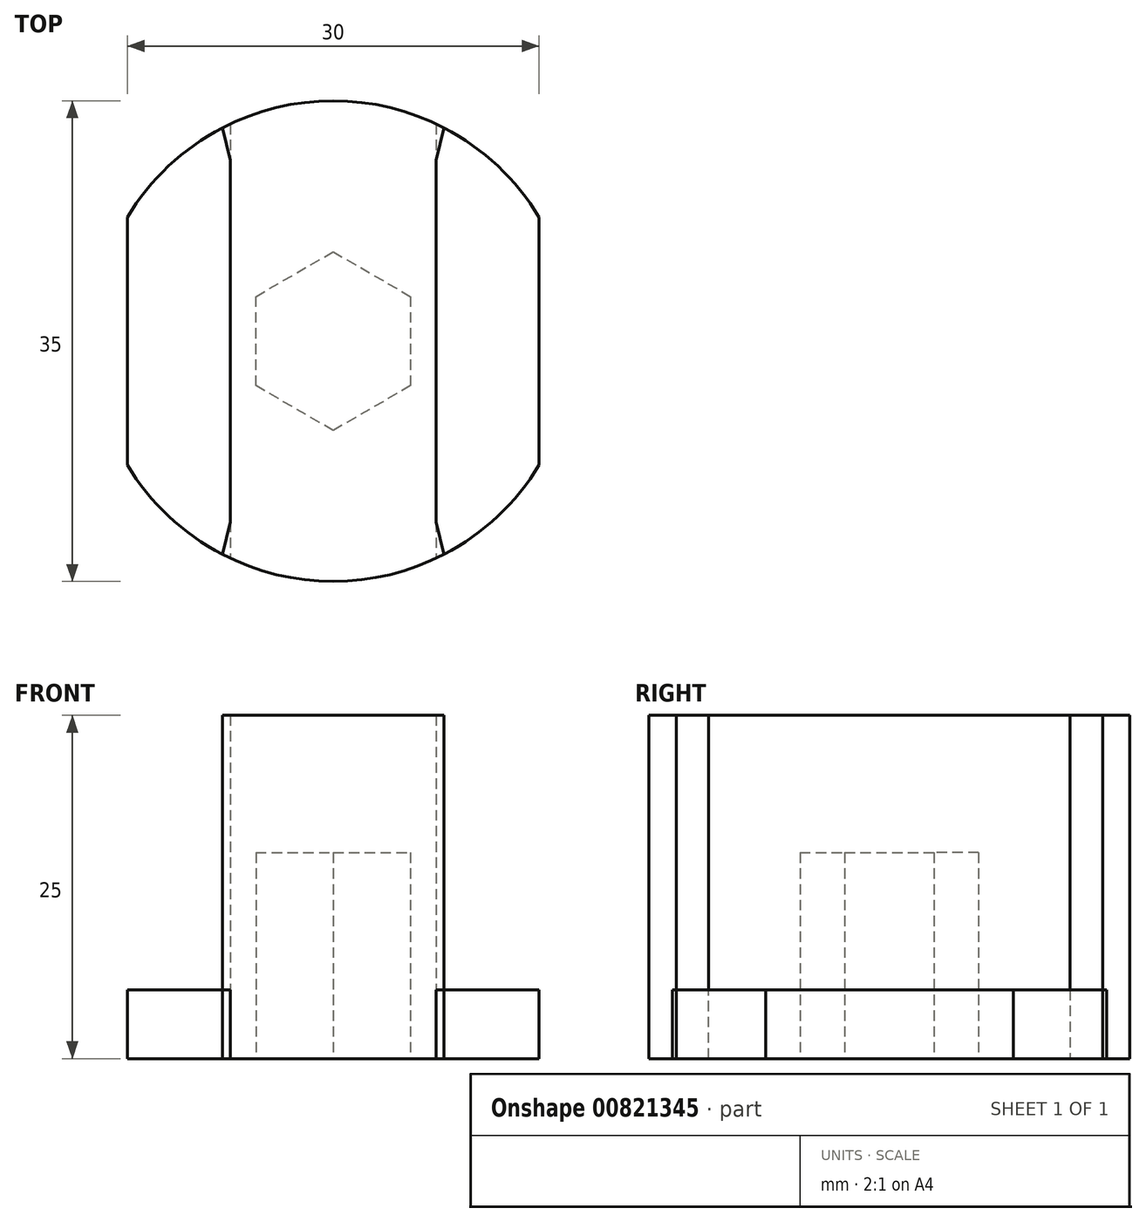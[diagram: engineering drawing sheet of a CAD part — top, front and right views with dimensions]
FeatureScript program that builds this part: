
annotation { "Feature Type Name" : "Feature", "Feature Type Description" : "" }
export const myFeature = defineFeature(function(context is Context, id is Id, definition is map)
    precondition{}
    {
        {
            var Q0;
            Q0=qCreatedBy(makeId("Top.planeOp"),FACE);
            var sketch = newSketch(context, id + "F0", { "sketchPlane" : qUnion([Q0])});
            skCircle(sketch, "E0", {"center": v(0, 0) * mm, "radius": 17.5 * mm});
            skLineSegment(sketch, "E1.bottom", {"start": v(7.5, 20) * mm, "end": v(-7.5, 20) * mm});
            skLineSegment(sketch, "E1.top", {"start": v(7.5, -20) * mm, "end": v(-7.5, -20) * mm});
            skLineSegment(sketch, "E1.left", {"start": v(7.5, 20) * mm, "end": v(7.5, -20) * mm});
            skLineSegment(sketch, "E1.right", {"start": v(-7.5, 20) * mm, "end": v(-7.5, -20) * mm});
            skLineSegment(sketch, "E2.bottom", {"start": v(15, 20) * mm, "end": v(-15, 20) * mm});
            skLineSegment(sketch, "E2.top", {"start": v(15, -20) * mm, "end": v(-15, -20) * mm});
            skLineSegment(sketch, "E2.left", {"start": v(15, 20) * mm, "end": v(15, -20) * mm});
            skLineSegment(sketch, "E2.right", {"start": v(-15, 20) * mm, "end": v(-15, -20) * mm});
            skLineSegment(sketch, "E3.bottom", {"start": v(23.86, 11.75) * mm, "end": v(-23.86, 11.75) * mm});
            skLineSegment(sketch, "E3.top", {"start": v(23.86, -11.75) * mm, "end": v(-23.86, -11.75) * mm});
            skLineSegment(sketch, "E3.left", {"start": v(23.86, 11.75) * mm, "end": v(23.86, -11.75) * mm});
            skLineSegment(sketch, "E3.right", {"start": v(-23.86, 11.75) * mm, "end": v(-23.86, -11.75) * mm});
            skLineSegment(sketch, "E4", {"start": v(0, 0) * mm, "end": v(0, 6.5) * mm});
            skCircle(sketch, "E5.cCircle", {"center": v(0, 0) * mm, "radius": 6.5 * mm, "construction": true});
            skLineSegment(sketch, "E5.0", {"start": v(0, 6.5) * mm, "end": v(5.63, 3.25) * mm});
            skLineSegment(sketch, "E5.1", {"start": v(5.63, 3.25) * mm, "end": v(5.63, -3.25) * mm});
            skLineSegment(sketch, "E5.2", {"start": v(5.63, -3.25) * mm, "end": v(0, -6.5) * mm});
            skLineSegment(sketch, "E5.3", {"start": v(0, -6.5) * mm, "end": v(-5.63, -3.25) * mm});
            skLineSegment(sketch, "E5.4", {"start": v(-5.63, -3.25) * mm, "end": v(-5.63, 3.25) * mm});
            skLineSegment(sketch, "E5.5", {"start": v(-5.63, 3.25) * mm, "end": v(0, 6.5) * mm});
            skSolve(sketch);
        }
        {
            var Q0;
            {var subQ0=sQuery(id+"F0.wireOp",EDGE,"E2.left");var subQ1=sQuery(id+"F0.wireOp",EDGE,"E0");var subQ2=makeQuery(id+"F0.imprint","INTERSECT",VERTEX,{"disambiguationData":[OD(0.0)],"derivedFrom":[subQ1,subQ0]});Q0=makeQuery(id+"F0.imprint","IMPRINT",FACE,{"disambiguationData":[TD([[makeQuery(id+"F0.imprint","IMPRINT",EDGE,{"disambiguationData":[TD([[subQ2,-1.0]])],"derivedFrom":subQ1}),1.0]])]});}
            var Q1;
            {var subQ0=sQuery(id+"F0.wireOp",EDGE,"E2.right");var subQ1=sQuery(id+"F0.wireOp",EDGE,"E0");var subQ2=makeQuery(id+"F0.imprint","INTERSECT",VERTEX,{"disambiguationData":[OD(0.0)],"derivedFrom":[subQ1,subQ0]});Q1=makeQuery(id+"F0.imprint","IMPRINT",FACE,{"disambiguationData":[TD([[makeQuery(id+"F0.imprint","IMPRINT",EDGE,{"disambiguationData":[TD([[subQ2,1.0]])],"derivedFrom":subQ1}),1.0]])]});}
            var Q2;
            {var subQ0=sQuery(id+"F0.wireOp",EDGE,"E1.right");var subQ1=sQuery(id+"F0.wireOp",EDGE,"E0");var subQ2=makeQuery(id+"F0.imprint","INTERSECT",VERTEX,{"disambiguationData":[OD(0.0)],"derivedFrom":[subQ1,subQ0]});Q2=makeQuery(id+"F0.imprint","IMPRINT",FACE,{"disambiguationData":[TD([[makeQuery(id+"F0.imprint","IMPRINT",EDGE,{"disambiguationData":[TD([[subQ2,-1.0]])],"derivedFrom":subQ1}),1.0]])]});}
            var Q3;
            {var subQ0=sQuery(id+"F0.wireOp",EDGE,"E1.left");var subQ1=sQuery(id+"F0.wireOp",EDGE,"E0");var subQ2=makeQuery(id+"F0.imprint","INTERSECT",VERTEX,{"disambiguationData":[OD(1.0)],"derivedFrom":[subQ1,subQ0]});Q3=makeQuery(id+"F0.imprint","IMPRINT",FACE,{"disambiguationData":[TD([[makeQuery(id+"F0.imprint","IMPRINT",EDGE,{"disambiguationData":[TD([[subQ2,-1.0]])],"derivedFrom":subQ1}),1.0]])]});}
            var Q4;
            {var subQ0=sQuery(id+"F0.wireOp",EDGE,"E3.top");var subQ1=sQuery(id+"F0.wireOp",EDGE,"E0");var subQ2=makeQuery(id+"F0.imprint","INTERSECT",VERTEX,{"disambiguationData":[OD(0.0)],"derivedFrom":[subQ1,subQ0]});Q4=makeQuery(id+"F0.imprint","IMPRINT",FACE,{"disambiguationData":[TD([[makeQuery(id+"F0.imprint","IMPRINT",EDGE,{"disambiguationData":[TD([[subQ2,-1.0]])],"derivedFrom":subQ1}),1.0]])]});}
            var Q5;
            {var subQ0=sQuery(id+"F0.wireOp",EDGE,"E3.bottom");var subQ1=sQuery(id+"F0.wireOp",EDGE,"E0");var subQ2=makeQuery(id+"F0.imprint","INTERSECT",VERTEX,{"disambiguationData":[OD(0.0)],"derivedFrom":[subQ1,subQ0]});Q5=makeQuery(id+"F0.imprint","IMPRINT",FACE,{"disambiguationData":[TD([[makeQuery(id+"F0.imprint","IMPRINT",EDGE,{"disambiguationData":[TD([[subQ2,-1.0]])],"derivedFrom":subQ1}),1.0]])]});}
            extrude(context, id + "F1", {"entities" : qUnion([Q0, Q1, Q2, Q3, Q4, Q5]), "depth" : 5 * mm, "offsetDistance" : 25 * mm});
        }
        {
            var Q0;
            Q0=makeQuery(id+"F0.imprint","IMPRINT",FACE,{"disambiguationData":[TD([[makeQuery(id+"F0.imprint","IMPRINT",EDGE,{"derivedFrom":sQuery(id+"F0.wireOp",EDGE,"VkzLpiYD-BapX-SKoB-1HIT-Cqfo4kMJtnIh.bottom")}),1.0]])]});
            var Q1;
            Q1=makeQuery(id+"F0.imprint","IMPRINT",FACE,{"disambiguationData":[TD([[makeQuery(id+"F0.imprint","IMPRINT",EDGE,{"derivedFrom":sQuery(id+"F0.wireOp",EDGE,"VkzLpiYD-BapX-SKoB-1HIT-Cqfo4kMJtnIh.bottom")}),-1.0]])]});
            var Q2;
            {var subQ0=sQuery(id+"F0.wireOp",EDGE,"E3.bottom");var subQ1=sQuery(id+"F0.wireOp",EDGE,"E1.right");var subQ2=makeQuery(id+"F0.imprint","INTERSECT",VERTEX,{"derivedFrom":[subQ1,subQ0]});Q2=makeQuery(id+"F0.imprint","IMPRINT",FACE,{"disambiguationData":[TD([[makeQuery(id+"F0.imprint","IMPRINT",EDGE,{"disambiguationData":[TD([[subQ2,-1.0]])],"derivedFrom":subQ1}),1.0]])]});}
            var Q3;
            {var subQ9=sQuery(id+"F0.wireOp",EDGE,"VkzLpiYD-BapX-SKoB-1HIT-Cqfo4kMJtnIh.top");Q3=makeQuery(id+"F0.imprint","IMPRINT",FACE,{"disambiguationData":[TD([[makeQuery(id+"F0.imprint","IMPRINT",EDGE,{"derivedFrom":subQ9}),1.0]])]});}
            var Q4;
            {var subQ0=sQuery(id+"F0.wireOp",EDGE,"E3.bottom");var subQ1=sQuery(id+"F0.wireOp",EDGE,"E1.left");var subQ2=makeQuery(id+"F0.imprint","INTERSECT",VERTEX,{"derivedFrom":[subQ1,subQ0]});Q4=makeQuery(id+"F0.imprint","IMPRINT",FACE,{"disambiguationData":[TD([[makeQuery(id+"F0.imprint","IMPRINT",EDGE,{"disambiguationData":[TD([[subQ2,-1.0]])],"derivedFrom":subQ1}),-1.0]])]});}
            var Q5;
            {var subQ0=sQuery(id+"F0.wireOp",EDGE,"E3.bottom");var subQ1=sQuery(id+"F0.wireOp",EDGE,"VkzLpiYD-BapX-SKoB-1HIT-Cqfo4kMJtnIh.left");var subQ2=makeQuery(id+"F0.imprint","INTERSECT",VERTEX,{"derivedFrom":[subQ1,subQ0]});Q5=makeQuery(id+"F0.imprint","IMPRINT",FACE,{"disambiguationData":[TD([[makeQuery(id+"F0.imprint","IMPRINT",EDGE,{"disambiguationData":[TD([[subQ2,-1.0]])],"derivedFrom":subQ1}),-1.0]])]});}
            var Q6;
            {var subQ0=sQuery(id+"F0.wireOp",EDGE,"VkzLpiYD-BapX-SKoB-1HIT-Cqfo4kMJtnIh.top");Q6=makeQuery(id+"F0.imprint","IMPRINT",FACE,{"disambiguationData":[TD([[makeQuery(id+"F0.imprint","IMPRINT",EDGE,{"derivedFrom":subQ0}),-1.0]])]});}
            var Q7;
            {var subQ0=sQuery(id+"F0.wireOp",EDGE,"E3.top");var subQ1=sQuery(id+"F0.wireOp",EDGE,"E0");var subQ2=makeQuery(id+"F0.imprint","INTERSECT",VERTEX,{"disambiguationData":[OD(0.0)],"derivedFrom":[subQ1,subQ0]});Q7=makeQuery(id+"F0.imprint","IMPRINT",FACE,{"disambiguationData":[TD([[makeQuery(id+"F0.imprint","IMPRINT",EDGE,{"disambiguationData":[TD([[subQ2,-1.0]])],"derivedFrom":subQ1}),1.0]])]});}
            var Q8;
            {var subQ0=sQuery(id+"F0.wireOp",EDGE,"E1.right");var subQ1=sQuery(id+"F0.wireOp",EDGE,"E0");var subQ2=makeQuery(id+"F0.imprint","INTERSECT",VERTEX,{"disambiguationData":[OD(0.0)],"derivedFrom":[subQ1,subQ0]});Q8=makeQuery(id+"F0.imprint","IMPRINT",FACE,{"disambiguationData":[TD([[makeQuery(id+"F0.imprint","IMPRINT",EDGE,{"disambiguationData":[TD([[subQ2,-1.0]])],"derivedFrom":subQ1}),1.0]])]});}
            var Q9;
            {var subQ0=sQuery(id+"F0.wireOp",EDGE,"E3.bottom");var subQ1=sQuery(id+"F0.wireOp",EDGE,"E0");var subQ2=makeQuery(id+"F0.imprint","INTERSECT",VERTEX,{"disambiguationData":[OD(0.0)],"derivedFrom":[subQ1,subQ0]});Q9=makeQuery(id+"F0.imprint","IMPRINT",FACE,{"disambiguationData":[TD([[makeQuery(id+"F0.imprint","IMPRINT",EDGE,{"disambiguationData":[TD([[subQ2,-1.0]])],"derivedFrom":subQ1}),1.0]])]});}
            var Q10;
            {var subQ0=sQuery(id+"F0.wireOp",EDGE,"E1.left");var subQ1=sQuery(id+"F0.wireOp",EDGE,"E0");var subQ2=makeQuery(id+"F0.imprint","INTERSECT",VERTEX,{"disambiguationData":[OD(1.0)],"derivedFrom":[subQ1,subQ0]});Q10=makeQuery(id+"F0.imprint","IMPRINT",FACE,{"disambiguationData":[TD([[makeQuery(id+"F0.imprint","IMPRINT",EDGE,{"disambiguationData":[TD([[subQ2,-1.0]])],"derivedFrom":subQ1}),1.0]])]});}
            var Q11;
            {var subQ0=sQuery(id+"F0.wireOp",EDGE,"E1.left");var subQ1=sQuery(id+"F0.wireOp",EDGE,"E0");var subQ2=makeQuery(id+"F0.imprint","INTERSECT",VERTEX,{"disambiguationData":[OD(0.0)],"derivedFrom":[subQ1,subQ0]});Q11=makeQuery(id+"F0.imprint","IMPRINT",FACE,{"disambiguationData":[TD([[makeQuery(id+"F0.imprint","IMPRINT",EDGE,{"disambiguationData":[TD([[subQ2,-1.0]])],"derivedFrom":subQ1}),1.0]])]});}
            var Q12;
            {var subQ0=sQuery(id+"F0.wireOp",EDGE,"E1.right");var subQ1=sQuery(id+"F0.wireOp",EDGE,"E0");var subQ2=makeQuery(id+"F0.imprint","INTERSECT",VERTEX,{"disambiguationData":[OD(1.0)],"derivedFrom":[subQ1,subQ0]});Q12=makeQuery(id+"F0.imprint","IMPRINT",FACE,{"disambiguationData":[TD([[makeQuery(id+"F0.imprint","IMPRINT",EDGE,{"disambiguationData":[TD([[subQ2,-1.0]])],"derivedFrom":subQ1}),1.0]])]});}
            var Q13;
            Q13=makeQuery(id+"F0.imprint","IMPRINT",FACE,{"disambiguationData":[TD([[makeQuery(id+"F0.imprint","IMPRINT",EDGE,{"derivedFrom":sQuery(id+"F0.wireOp",EDGE,"E5.0")}),-1.0]])]});
            extrude(context, id + "F2", {"entities" : qUnion([Q0, Q1, Q2, Q3, Q4, Q5, Q6, Q7, Q8, Q9, Q10, Q11, Q12, Q13]), "depth" : 25 * mm, "offsetDistance" : 25 * mm});
        }
        {
            var Q0;
            {var subQ0=sQuery(id+"F0.wireOp",EDGE,"E3.top");var subQ1=sQuery(id+"F0.wireOp",EDGE,"E0");Q0=makeQuery(id+"F2.opExtrude","SWEPT_EDGE",EDGE,{"disambiguationData":[OSD([subQ1,subQ0]),TDD([makeQuery(id+"F0.imprint","INTERSECT",VERTEX,{"disambiguationData":[OD(0.0)],"derivedFrom":[subQ1,subQ0]})])]});}
            var Q1;
            {var subQ0=sQuery(id+"F0.wireOp",EDGE,"E3.top");var subQ1=sQuery(id+"F0.wireOp",EDGE,"E0");Q1=makeQuery(id+"F2.opExtrude","SWEPT_EDGE",EDGE,{"disambiguationData":[OSD([subQ1,subQ0]),TDD([makeQuery(id+"F0.imprint","INTERSECT",VERTEX,{"disambiguationData":[OD(1.0)],"derivedFrom":[subQ1,subQ0]})])]});}
            var Q2;
            {var subQ0=sQuery(id+"F0.wireOp",EDGE,"E3.bottom");var subQ1=sQuery(id+"F0.wireOp",EDGE,"E0");Q2=makeQuery(id+"F2.opExtrude","SWEPT_EDGE",EDGE,{"disambiguationData":[OSD([subQ1,subQ0]),TDD([makeQuery(id+"F0.imprint","INTERSECT",VERTEX,{"disambiguationData":[OD(0.0)],"derivedFrom":[subQ1,subQ0]})])]});}
            var Q3;
            {var subQ0=sQuery(id+"F0.wireOp",EDGE,"E3.bottom");var subQ1=sQuery(id+"F0.wireOp",EDGE,"E0");Q3=makeQuery(id+"F2.opExtrude","SWEPT_EDGE",EDGE,{"disambiguationData":[OSD([subQ1,subQ0]),TDD([makeQuery(id+"F0.imprint","INTERSECT",VERTEX,{"disambiguationData":[OD(1.0)],"derivedFrom":[subQ1,subQ0]})])]});}
            chamfer(context, id + "F3", {"entities" : qUnion([Q0, Q1, Q2, Q3]), "width" : 2 * mm, "tangentPropagation" : true});
        }
        {
            var Q0;
            Q0=makeQuery(id+"F0.imprint","IMPRINT",FACE,{"disambiguationData":[TD([[makeQuery(id+"F0.imprint","IMPRINT",EDGE,{"derivedFrom":sQuery(id+"F0.wireOp",EDGE,"E5.0")}),-1.0]])]});
            var Q1;
            Q1=makeQuery(id+"F0.imprint","IMPRINT",FACE,{"disambiguationData":[TD([[makeQuery(id+"F0.imprint","IMPRINT",EDGE,{"derivedFrom":sQuery(id+"F0.wireOp",EDGE,"E5.0")}),-1.0]])]});
            extrude(context, id + "F4", {"entities" : qUnion([Q0, Q1]), "operationType" : NewBodyOperationType.REMOVE, "oppositeDirection" : true, "depth" : -15 * mm, "offsetDistance" : 25 * mm});
        }
    });
